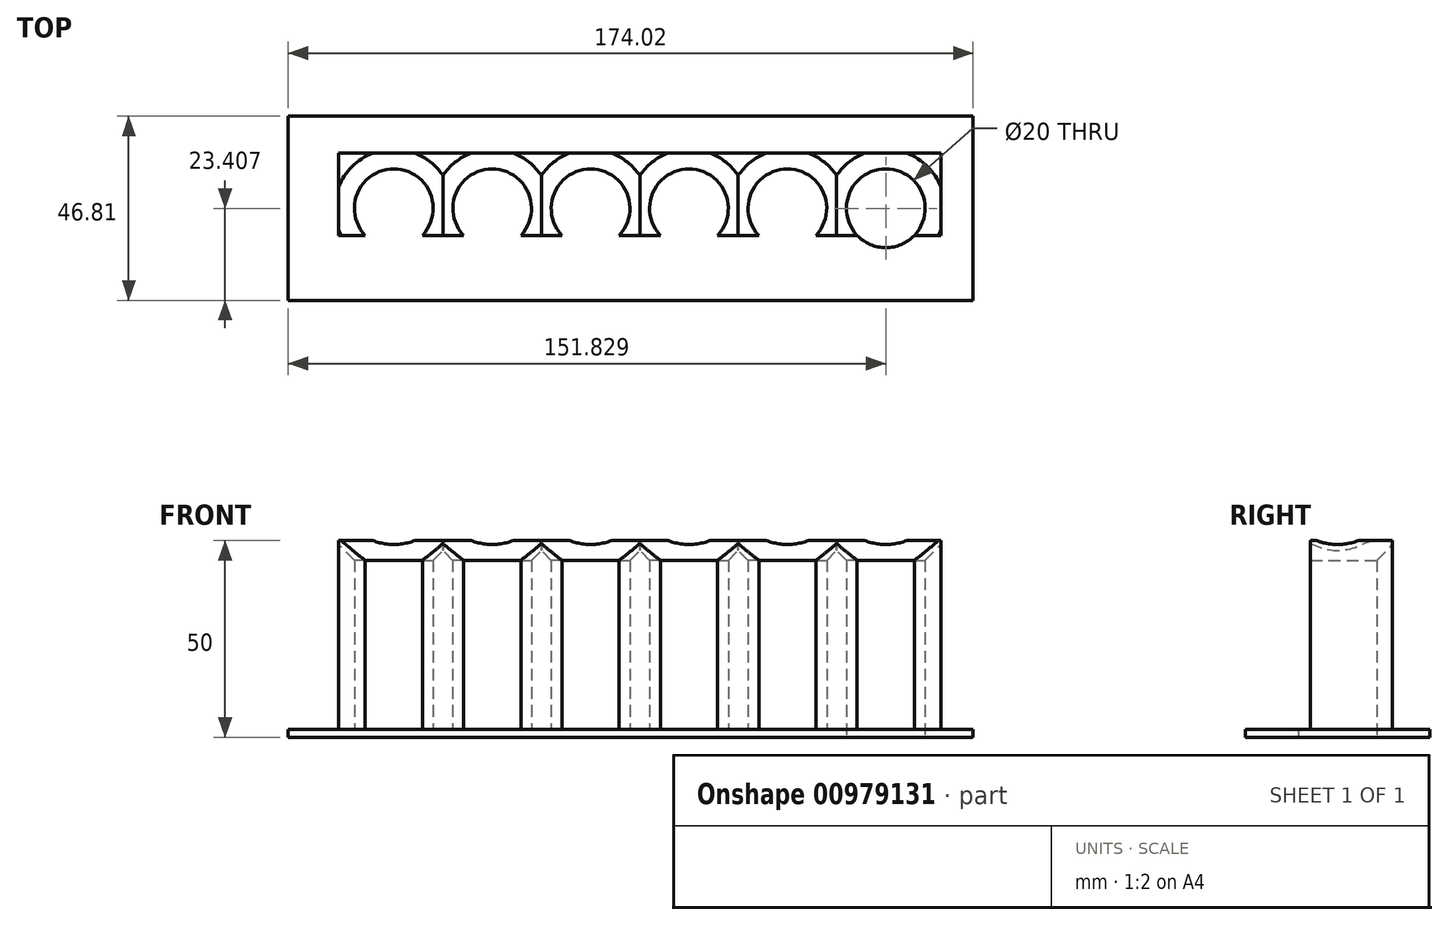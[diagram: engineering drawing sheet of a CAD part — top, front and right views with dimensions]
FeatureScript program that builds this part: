
annotation { "Feature Type Name" : "Feature", "Feature Type Description" : "" }
export const myFeature = defineFeature(function(context is Context, id is Id, definition is map)
    precondition{}
    {
        {
            var Q0;
            Q0=qCreatedBy(makeId("Top.planeOp"),FACE);
            var sketch = newSketch(context, id + "F0", { "sketchPlane" : qUnion([Q0])});
            skCircle(sketch, "E0", {"center": v(-56.08, 30.98) * mm, "radius": 10 * mm});
            skCircle(sketch, "E1.1.0.0", {"center": v(-31.08, 30.98) * mm, "radius": 10 * mm});
            skCircle(sketch, "E1.2.0.0", {"center": v(-6.08, 30.98) * mm, "radius": 10 * mm});
            skCircle(sketch, "E1.3.0.0", {"center": v(18.92, 30.98) * mm, "radius": 10 * mm});
            skCircle(sketch, "E1.4.0.0", {"center": v(43.92, 30.98) * mm, "radius": 10 * mm});
            skCircle(sketch, "E1.5.0.0", {"center": v(68.92, 30.98) * mm, "radius": 10 * mm});
            skLineSegment(sketch, "E1.direction1", {"start": v(-56.08, 30.98) * mm, "end": v(-31.08, 30.98) * mm, "construction": true});
            skLineSegment(sketch, "E2.bottom", {"start": v(-70.08, 44.98) * mm, "end": v(82.92, 44.98) * mm});
            skLineSegment(sketch, "E2.top", {"start": v(-70.08, 16.98) * mm, "end": v(82.92, 16.98) * mm});
            skLineSegment(sketch, "E2.left", {"start": v(-70.08, 44.98) * mm, "end": v(-70.08, 16.98) * mm});
            skLineSegment(sketch, "E2.right", {"start": v(82.92, 44.98) * mm, "end": v(82.92, 16.98) * mm});
            skLineSegment(sketch, "E3", {"start": v(-70.08, 24.11) * mm, "end": v(82.92, 24.11) * mm});
            skLineSegment(sketch, "E4.bottom", {"start": v(-82.91, 54.38) * mm, "end": v(91.1, 54.38) * mm});
            skLineSegment(sketch, "E4.top", {"start": v(-82.91, 7.57) * mm, "end": v(91.1, 7.57) * mm});
            skLineSegment(sketch, "E4.left", {"start": v(-82.91, 54.38) * mm, "end": v(-82.91, 7.57) * mm});
            skLineSegment(sketch, "E4.right", {"start": v(91.1, 54.38) * mm, "end": v(91.1, 7.57) * mm});
            skSolve(sketch);
        }
        {
            var Q0;
            {var subQ7=sQuery(id+"F0.wireOp",EDGE,"E2.bottom");Q0=makeQuery(id+"F0.imprint","IMPRINT",FACE,{"disambiguationData":[TD([[makeQuery(id+"F0.imprint","IMPRINT",EDGE,{"derivedFrom":subQ7}),-1.0]])]});}
            extrude(context, id + "F1", {"entities" : qUnion([Q0]), "depth" : 50 * mm, "offsetDistance" : 25 * mm});
        }
        {
            var Q0;
            {var subQ4=sQuery(id+"F0.wireOp",EDGE,"E2.bottom");Q0=makeQuery(id+"F0.imprint","IMPRINT",FACE,{"disambiguationData":[TD([[makeQuery(id+"F0.imprint","IMPRINT",EDGE,{"derivedFrom":subQ4}),1.0]])]});}
            var Q1;
            {var subQ12=sQuery(id+"F0.wireOp",EDGE,"E2.top");Q1=makeQuery(id+"F0.imprint","IMPRINT",FACE,{"disambiguationData":[TD([[makeQuery(id+"F0.imprint","IMPRINT",EDGE,{"derivedFrom":subQ12}),1.0]])]});}
            var Q2;
            {var subQ0=sQuery(id+"F0.wireOp",EDGE,"E3");var subQ1=sQuery(id+"F0.wireOp",EDGE,"E0");var subQ2=makeQuery(id+"F0.imprint","INTERSECT",VERTEX,{"disambiguationData":[OD(0.0)],"derivedFrom":[subQ1,subQ0]});Q2=makeQuery(id+"F0.imprint","IMPRINT",FACE,{"disambiguationData":[TD([[makeQuery(id+"F0.imprint","IMPRINT",EDGE,{"disambiguationData":[TD([[subQ2,1.0]])],"derivedFrom":subQ1}),1.0]])]});}
            var Q3;
            {var subQ0=sQuery(id+"F0.wireOp",EDGE,"E3");var subQ1=sQuery(id+"F0.wireOp",EDGE,"E0");var subQ2=makeQuery(id+"F0.imprint","INTERSECT",VERTEX,{"disambiguationData":[OD(0.0)],"derivedFrom":[subQ1,subQ0]});Q3=makeQuery(id+"F0.imprint","IMPRINT",FACE,{"disambiguationData":[TD([[makeQuery(id+"F0.imprint","IMPRINT",EDGE,{"disambiguationData":[TD([[subQ2,-1.0]])],"derivedFrom":subQ1}),1.0]])]});}
            var Q4;
            {var subQ0=sQuery(id+"F0.wireOp",EDGE,"E3");var subQ1=sQuery(id+"F0.wireOp",EDGE,"E1.1.0.0");var subQ2=makeQuery(id+"F0.imprint","INTERSECT",VERTEX,{"disambiguationData":[OD(0.0)],"derivedFrom":[subQ1,subQ0]});Q4=makeQuery(id+"F0.imprint","IMPRINT",FACE,{"disambiguationData":[TD([[makeQuery(id+"F0.imprint","IMPRINT",EDGE,{"disambiguationData":[TD([[subQ2,1.0]])],"derivedFrom":subQ1}),1.0]])]});}
            var Q5;
            {var subQ0=sQuery(id+"F0.wireOp",EDGE,"E3");var subQ1=sQuery(id+"F0.wireOp",EDGE,"E1.1.0.0");var subQ2=makeQuery(id+"F0.imprint","INTERSECT",VERTEX,{"disambiguationData":[OD(0.0)],"derivedFrom":[subQ1,subQ0]});Q5=makeQuery(id+"F0.imprint","IMPRINT",FACE,{"disambiguationData":[TD([[makeQuery(id+"F0.imprint","IMPRINT",EDGE,{"disambiguationData":[TD([[subQ2,-1.0]])],"derivedFrom":subQ1}),1.0]])]});}
            var Q6;
            {var subQ0=sQuery(id+"F0.wireOp",EDGE,"E3");var subQ1=sQuery(id+"F0.wireOp",EDGE,"E1.2.0.0");var subQ2=makeQuery(id+"F0.imprint","INTERSECT",VERTEX,{"disambiguationData":[OD(0.0)],"derivedFrom":[subQ1,subQ0]});Q6=makeQuery(id+"F0.imprint","IMPRINT",FACE,{"disambiguationData":[TD([[makeQuery(id+"F0.imprint","IMPRINT",EDGE,{"disambiguationData":[TD([[subQ2,1.0]])],"derivedFrom":subQ1}),1.0]])]});}
            var Q7;
            {var subQ0=sQuery(id+"F0.wireOp",EDGE,"E3");var subQ1=sQuery(id+"F0.wireOp",EDGE,"E1.2.0.0");var subQ2=makeQuery(id+"F0.imprint","INTERSECT",VERTEX,{"disambiguationData":[OD(0.0)],"derivedFrom":[subQ1,subQ0]});Q7=makeQuery(id+"F0.imprint","IMPRINT",FACE,{"disambiguationData":[TD([[makeQuery(id+"F0.imprint","IMPRINT",EDGE,{"disambiguationData":[TD([[subQ2,-1.0]])],"derivedFrom":subQ1}),1.0]])]});}
            var Q8;
            {var subQ0=sQuery(id+"F0.wireOp",EDGE,"E3");var subQ1=sQuery(id+"F0.wireOp",EDGE,"E1.3.0.0");var subQ2=makeQuery(id+"F0.imprint","INTERSECT",VERTEX,{"disambiguationData":[OD(0.0)],"derivedFrom":[subQ1,subQ0]});Q8=makeQuery(id+"F0.imprint","IMPRINT",FACE,{"disambiguationData":[TD([[makeQuery(id+"F0.imprint","IMPRINT",EDGE,{"disambiguationData":[TD([[subQ2,1.0]])],"derivedFrom":subQ1}),1.0]])]});}
            var Q9;
            {var subQ0=sQuery(id+"F0.wireOp",EDGE,"E3");var subQ1=sQuery(id+"F0.wireOp",EDGE,"E1.3.0.0");var subQ2=makeQuery(id+"F0.imprint","INTERSECT",VERTEX,{"disambiguationData":[OD(0.0)],"derivedFrom":[subQ1,subQ0]});Q9=makeQuery(id+"F0.imprint","IMPRINT",FACE,{"disambiguationData":[TD([[makeQuery(id+"F0.imprint","IMPRINT",EDGE,{"disambiguationData":[TD([[subQ2,-1.0]])],"derivedFrom":subQ1}),1.0]])]});}
            var Q10;
            {var subQ0=sQuery(id+"F0.wireOp",EDGE,"E3");var subQ1=sQuery(id+"F0.wireOp",EDGE,"E1.4.0.0");var subQ2=makeQuery(id+"F0.imprint","INTERSECT",VERTEX,{"disambiguationData":[OD(0.0)],"derivedFrom":[subQ1,subQ0]});Q10=makeQuery(id+"F0.imprint","IMPRINT",FACE,{"disambiguationData":[TD([[makeQuery(id+"F0.imprint","IMPRINT",EDGE,{"disambiguationData":[TD([[subQ2,1.0]])],"derivedFrom":subQ1}),1.0]])]});}
            var Q11;
            {var subQ0=sQuery(id+"F0.wireOp",EDGE,"E3");var subQ1=sQuery(id+"F0.wireOp",EDGE,"E1.4.0.0");var subQ2=makeQuery(id+"F0.imprint","INTERSECT",VERTEX,{"disambiguationData":[OD(0.0)],"derivedFrom":[subQ1,subQ0]});Q11=makeQuery(id+"F0.imprint","IMPRINT",FACE,{"disambiguationData":[TD([[makeQuery(id+"F0.imprint","IMPRINT",EDGE,{"disambiguationData":[TD([[subQ2,-1.0]])],"derivedFrom":subQ1}),1.0]])]});}
            extrude(context, id + "F2", {"entities" : qUnion([Q0, Q1, Q2, Q3, Q4, Q5, Q6, Q7, Q8, Q9, Q10, Q11]), "operationType" : NewBodyOperationType.ADD, "depth" : 2 * mm, "offsetDistance" : 25 * mm});
        }
        {
            var Q0;
            Q0=makeQuery(id+"F1.opExtrude","CAP_EDGE",EDGE,{"disambiguationData":[OSD([sQuery(id+"F0.wireOp",EDGE,"E0")])],"isStart":false});
            var Q1;
            Q1=makeQuery(id+"F1.opExtrude","CAP_EDGE",EDGE,{"disambiguationData":[OSD([sQuery(id+"F0.wireOp",EDGE,"E1.1.0.0")])],"isStart":false});
            var Q2;
            Q2=makeQuery(id+"F1.opExtrude","CAP_EDGE",EDGE,{"disambiguationData":[OSD([sQuery(id+"F0.wireOp",EDGE,"E1.2.0.0")])],"isStart":false});
            var Q3;
            Q3=makeQuery(id+"F1.opExtrude","CAP_EDGE",EDGE,{"disambiguationData":[OSD([sQuery(id+"F0.wireOp",EDGE,"E1.3.0.0")])],"isStart":false});
            var Q4;
            Q4=makeQuery(id+"F1.opExtrude","CAP_EDGE",EDGE,{"disambiguationData":[OSD([sQuery(id+"F0.wireOp",EDGE,"E1.4.0.0")])],"isStart":false});
            var Q5;
            Q5=makeQuery(id+"F1.opExtrude","CAP_EDGE",EDGE,{"disambiguationData":[OSD([sQuery(id+"F0.wireOp",EDGE,"E1.5.0.0")])],"isStart":false});
            chamfer(context, id + "F3", {"entities" : qUnion([Q0, Q1, Q2, Q3, Q4, Q5]), "width" : 5 * mm, "tangentPropagation" : true});
        }
    });
